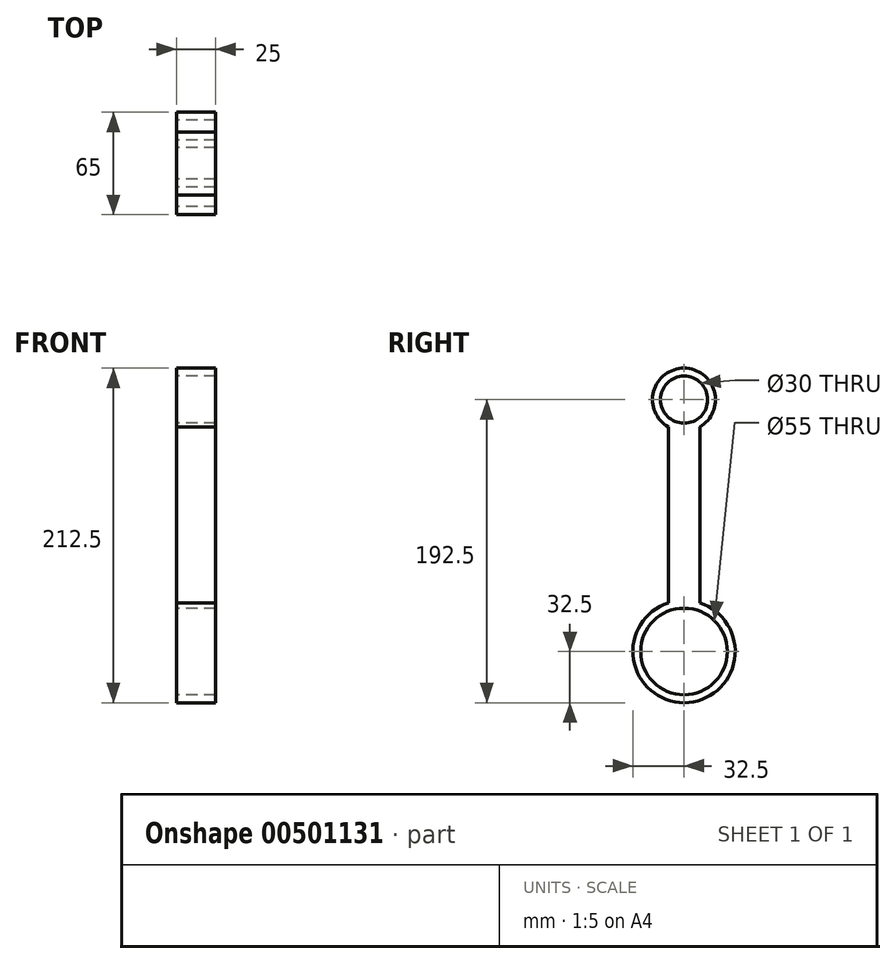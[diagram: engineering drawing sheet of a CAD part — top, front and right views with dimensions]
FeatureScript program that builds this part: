
annotation { "Feature Type Name" : "Feature", "Feature Type Description" : "" }
export const myFeature = defineFeature(function(context is Context, id is Id, definition is map)
    precondition{}
    {
        {
            var Q0;
            Q0=qCreatedBy(makeId("Right.planeOp"),FACE);
            var sketch = newSketch(context, id + "F0", { "sketchPlane" : qUnion([Q0])});
            skCircle(sketch, "E0", {"center": v(0, 80) * mm, "radius": 15 * mm});
            skCircle(sketch, "E1", {"center": v(0, -80) * mm, "radius": 27.5 * mm});
            skArc(sketch, "E2.0", {"start": v(10, 62.68) * mm, "mid": v(0, 100) * mm, "end": v(-10, 62.68) * mm});
            skArc(sketch, "E3.0", {"start": v(-10, -49.08) * mm, "mid": v(0, -112.5) * mm, "end": v(10, -49.08) * mm});
            skLineSegment(sketch, "E4", {"start": v(0, 80) * mm, "end": v(0, -80) * mm, "construction": true});
            skLineSegment(sketch, "E5.0", {"start": v(-10, 62.68) * mm, "end": v(-10, -49.08) * mm});
            skLineSegment(sketch, "E6.0", {"start": v(10, 62.68) * mm, "end": v(10, -49.08) * mm});
            skSolve(sketch);
        }
        {
            var Q0;
            Q0 = qSketchRegion(id + "F0", true);
            extrude(context, id + "F1", {"entities" : qUnion([Q0]), "endBound" : BoundingType.SYMMETRIC, "depth" : 25 * mm});
        }
    });
